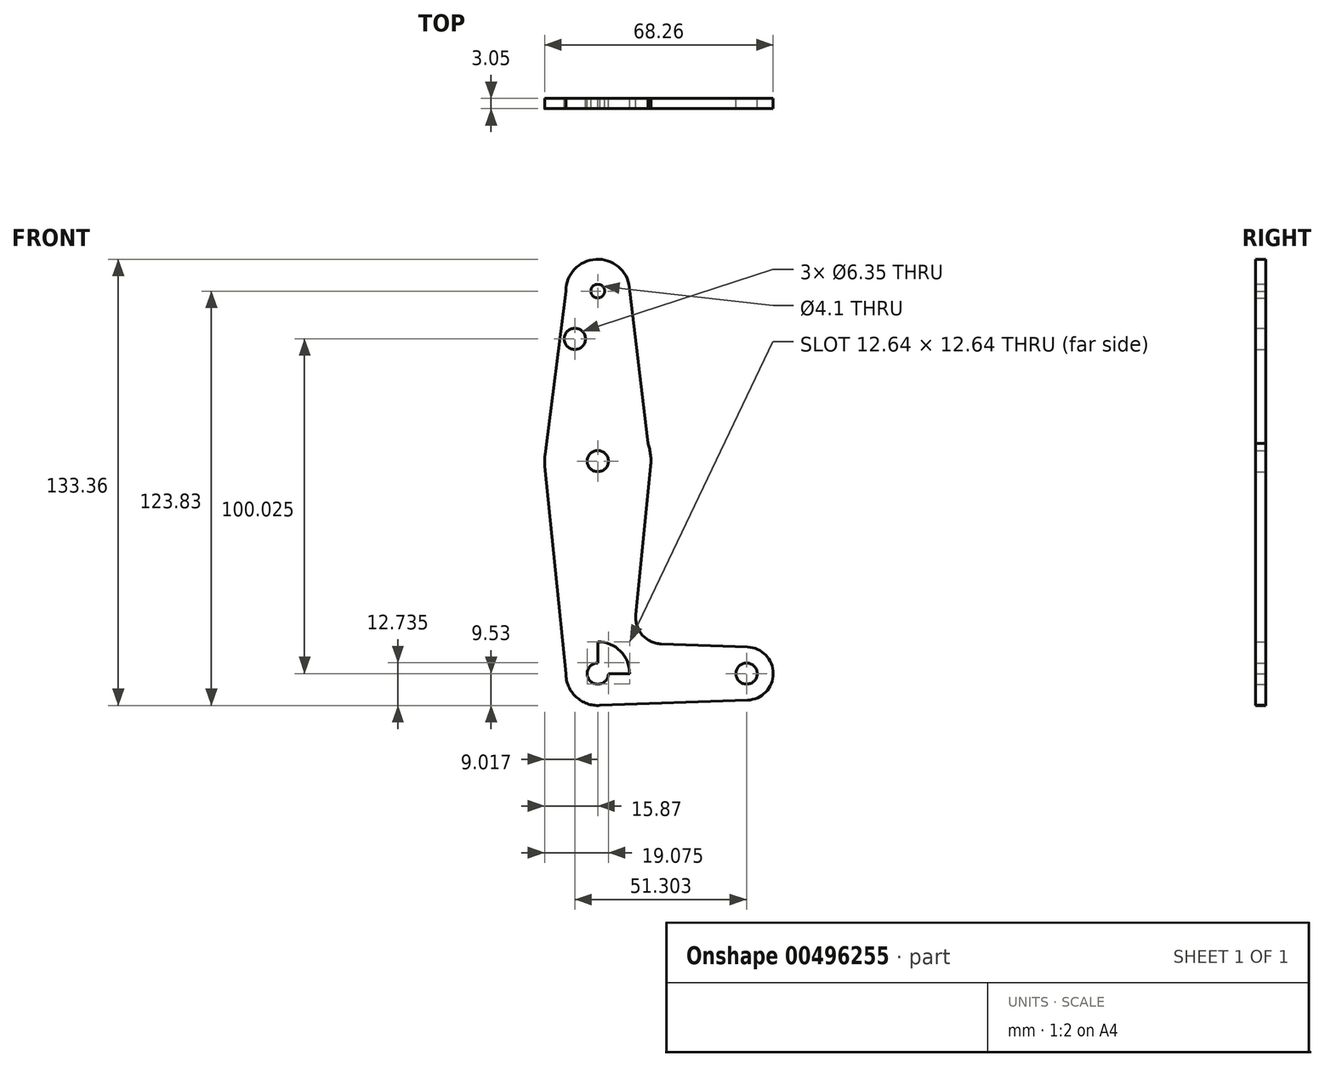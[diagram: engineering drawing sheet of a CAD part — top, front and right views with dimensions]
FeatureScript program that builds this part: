
annotation { "Feature Type Name" : "Feature", "Feature Type Description" : "" }
export const myFeature = defineFeature(function(context is Context, id is Id, definition is map)
    precondition{}
    {
        {
            var Q0;
            Q0=qCreatedBy(makeId("Front.planeOp"),FACE);
            var sketch = newSketch(context, id + "F0", { "sketchPlane" : qUnion([Q0])});
            skLineSegment(sketch, "E0", {"start": v(0, 0) * mm, "end": v(0, 114.3) * mm});
            skLineSegment(sketch, "E1", {"start": v(0, 0) * mm, "end": v(44.45, 0) * mm});
            skCircle(sketch, "E2", {"center": v(0, 114.3) * mm, "radius": 2.05 * mm});
            skCircle(sketch, "E3", {"center": v(0, 114.3) * mm, "radius": 9.53 * mm});
            skCircle(sketch, "E4", {"center": v(0, 63.5) * mm, "radius": 15.88 * mm});
            skCircle(sketch, "E5", {"center": v(0, 0) * mm, "radius": 9.53 * mm});
            skCircle(sketch, "E6", {"center": v(44.45, 0) * mm, "radius": 7.94 * mm});
            skLineSegment(sketch, "E7", {"start": v(-9.53, 114.3) * mm, "end": v(-15.75, 65.5) * mm});
            skLineSegment(sketch, "E8", {"start": v(9.46, 115.42) * mm, "end": v(15.8, 61.91) * mm});
            skLineSegment(sketch, "E9", {"start": v(15.8, 61.91) * mm, "end": v(11.34, 17.59) * mm});
            skLineSegment(sketch, "E10", {"start": v(18.97, 8.85) * mm, "end": v(44.73, 7.93) * mm});
            skLineSegment(sketch, "E11", {"start": v(-15.8, 61.9) * mm, "end": v(-9.53, 0) * mm});
            skLineSegment(sketch, "E12", {"start": v(0, -9.53) * mm, "end": v(44.73, -7.93) * mm});
            skCircle(sketch, "E13", {"center": v(-6.85, 100.03) * mm, "radius": 3.18 * mm});
            skCircle(sketch, "E14", {"center": v(0, 63.5) * mm, "radius": 3.18 * mm});
            skCircle(sketch, "E15", {"center": v(44.45, 0) * mm, "radius": 3.18 * mm});
            skPoint(sketch, "E16.newPointA", {"position": v(9.57, 0) * mm});
            skPoint(sketch, "E16.newPointB", {"position": v(0, 9.53) * mm});
            skArc(sketch, "E16.filletArc", {"start": v(11.34, 17.59) * mm, "mid": v(13.26, 11.57) * mm, "end": v(18.97, 8.85) * mm});
            skCircle(sketch, "E17", {"center": v(0, 0) * mm, "radius": 3.18 * mm});
            skSolve(sketch);
        }
        {
            var Q0;
            Q0 = qSketchRegion(id + "F0", true);
            extrude(context, id + "F1", {"entities" : qUnion([Q0]), "depth" : 3.05 * mm});
        }
    });
